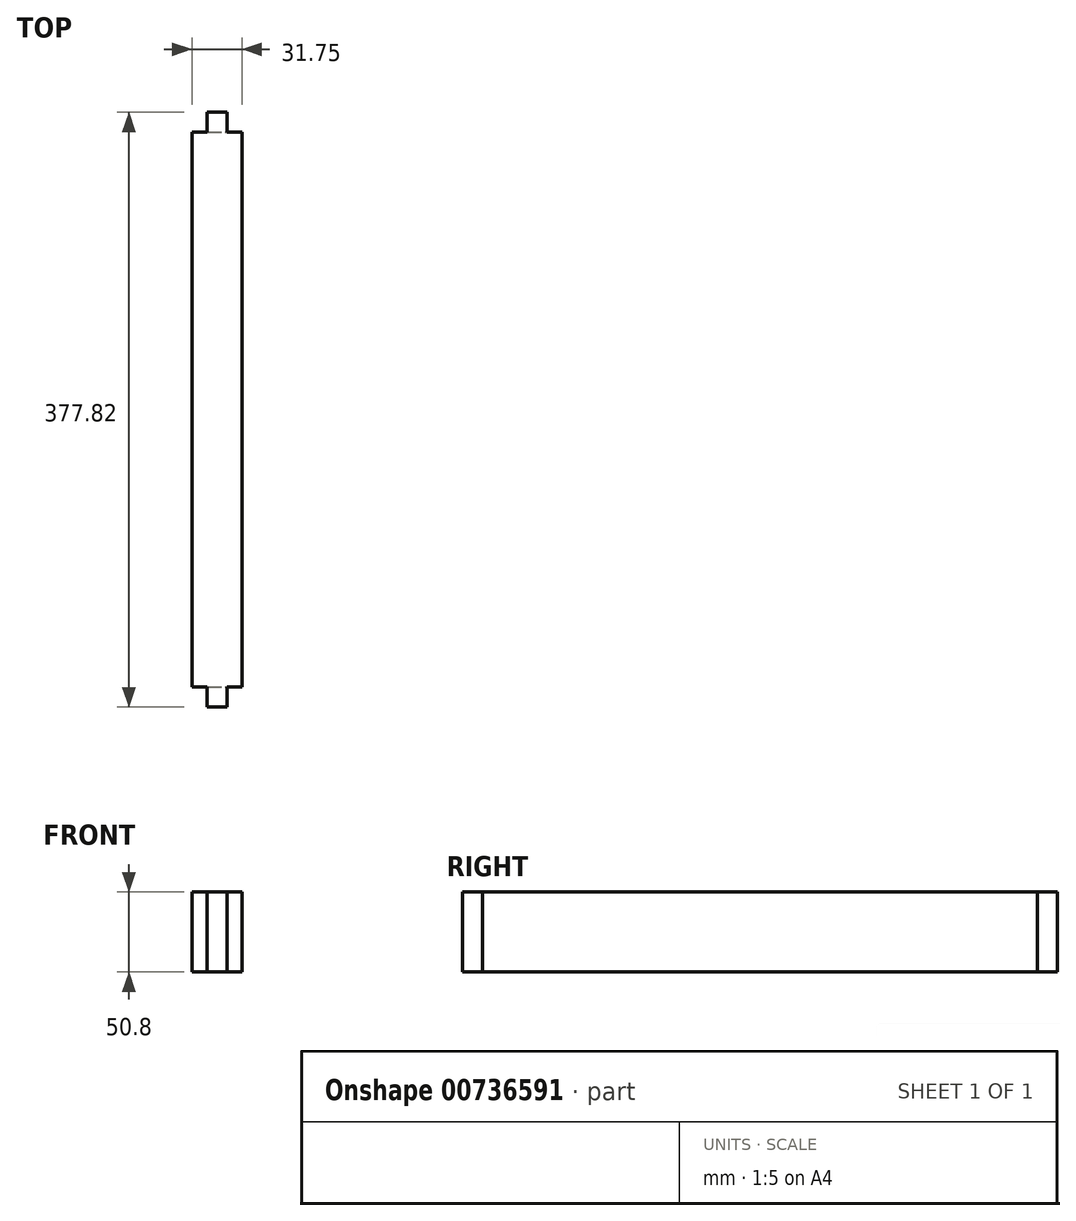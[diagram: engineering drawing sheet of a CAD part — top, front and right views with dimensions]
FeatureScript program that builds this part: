
annotation { "Feature Type Name" : "Feature", "Feature Type Description" : "" }
export const myFeature = defineFeature(function(context is Context, id is Id, definition is map)
    precondition{}
    {
        {
            var Q0;
            Q0=qCreatedBy(makeId("Front.planeOp"),FACE);
            var sketch = newSketch(context, id + "F0", { "sketchPlane" : qUnion([Q0])});
            skLineSegment(sketch, "E0.bottom", {"start": v(-25.86, 33.98) * mm, "end": v(5.9, 33.98) * mm});
            skLineSegment(sketch, "E0.top", {"start": v(-25.86, -16.82) * mm, "end": v(5.9, -16.82) * mm});
            skLineSegment(sketch, "E0.left", {"start": v(-25.86, 33.98) * mm, "end": v(-25.86, -16.82) * mm});
            skLineSegment(sketch, "E0.right", {"start": v(5.9, 33.98) * mm, "end": v(5.9, -16.82) * mm});
            skLineSegment(sketch, "E1.bottom", {"start": v(-16.33, -16.79) * mm, "end": v(-3.63, -16.79) * mm});
            skLineSegment(sketch, "E1.top", {"start": v(-16.33, 33.98) * mm, "end": v(-3.63, 33.98) * mm});
            skLineSegment(sketch, "E1.left", {"start": v(-16.33, -16.79) * mm, "end": v(-16.33, 33.98) * mm});
            skLineSegment(sketch, "E1.right", {"start": v(-3.63, -16.79) * mm, "end": v(-3.63, 33.98) * mm});
            skSolve(sketch);
        }
        {
            var Q0;
            Q0=makeQuery(id+"F0.imprint","IMPRINT",FACE,{"disambiguationData":[TD([[makeQuery(id+"F0.imprint","IMPRINT",EDGE,{"derivedFrom":sQuery(id+"F0.wireOp",EDGE,"E1.bottom")}),1.0]])]});
            extrude(context, id + "F1", {"entities" : qUnion([Q0]), "depth" : 12.7 * mm, "offsetDistance" : 25.4 * mm});
        }
        {
            var Q0;
            Q0=makeQuery(id+"F0.imprint","IMPRINT",FACE,{"disambiguationData":[TD([[makeQuery(id+"F0.imprint","IMPRINT",EDGE,{"derivedFrom":sQuery(id+"F0.wireOp",EDGE,"E1.bottom")}),1.0]])]});
            extrude(context, id + "F2", {"entities" : qUnion([Q0]), "operationType" : NewBodyOperationType.ADD, "oppositeDirection" : true, "depth" : 365.12 * mm, "offsetDistance" : 25.4 * mm});
        }
        {
            var Q0;
            Q0=makeQuery(id+"F0.imprint","IMPRINT",FACE,{"disambiguationData":[TD([[makeQuery(id+"F0.imprint","IMPRINT",EDGE,{"derivedFrom":sQuery(id+"F0.wireOp",EDGE,"E0.top")}),1.0]])]});
            extrude(context, id + "F3", {"entities" : qUnion([Q0]), "operationType" : NewBodyOperationType.ADD, "oppositeDirection" : true, "depth" : 352.42 * mm, "offsetDistance" : 25.4 * mm});
        }
    });
